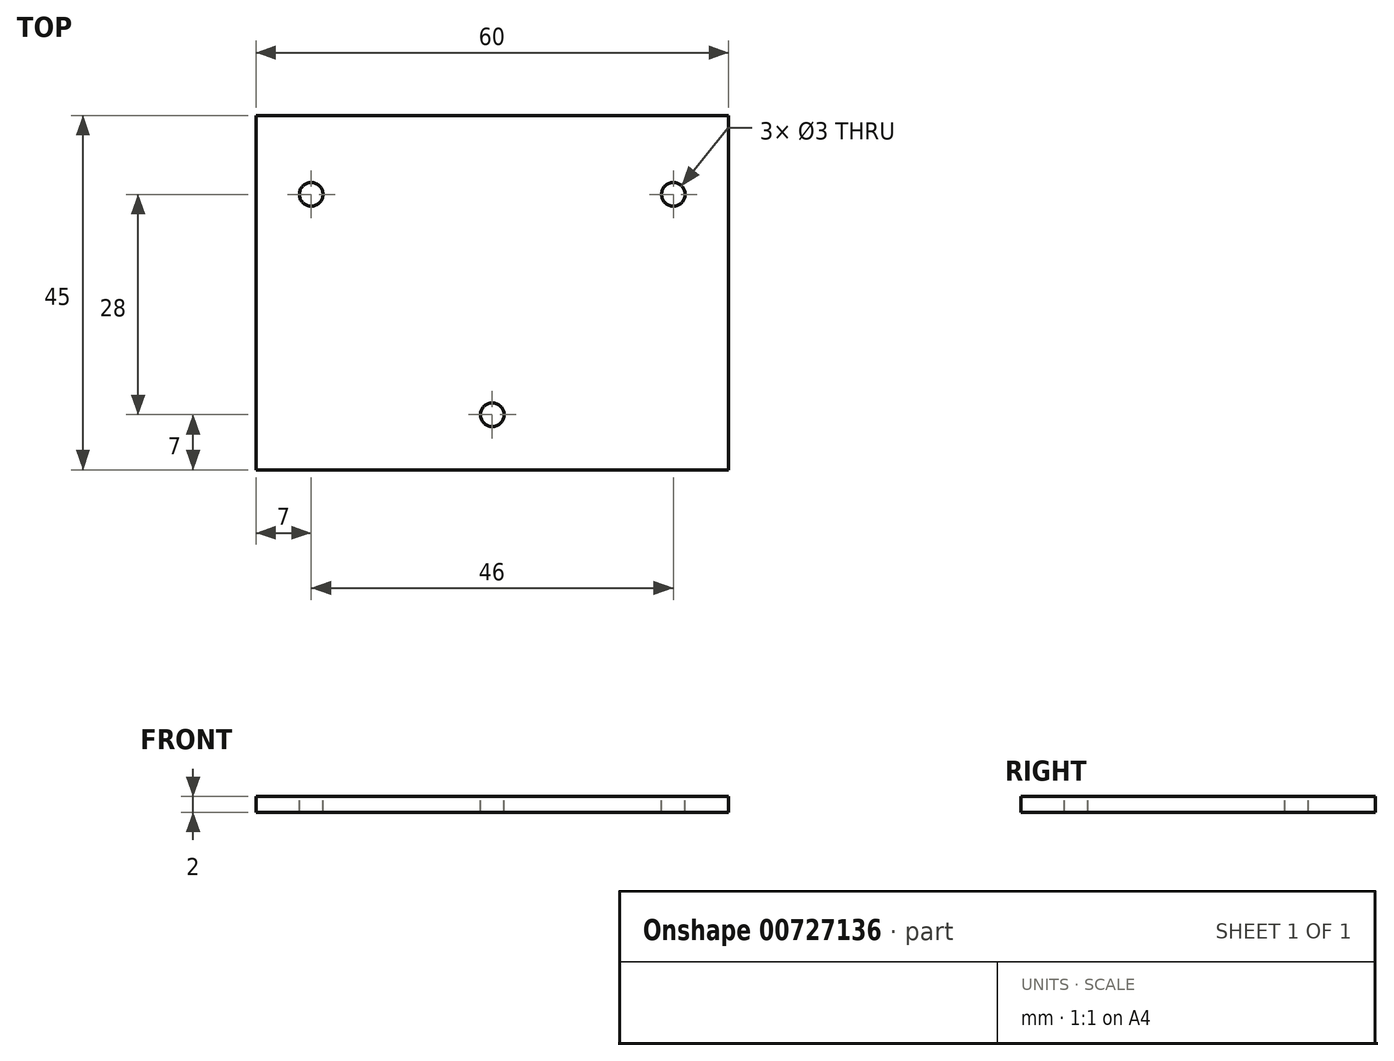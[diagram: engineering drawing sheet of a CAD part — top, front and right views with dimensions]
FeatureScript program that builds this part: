
annotation { "Feature Type Name" : "Feature", "Feature Type Description" : "" }
export const myFeature = defineFeature(function(context is Context, id is Id, definition is map)
    precondition{}
    {
        {
            var Q0;
            Q0=qCreatedBy(makeId("Top.planeOp"),FACE);
            var sketch = newSketch(context, id + "F0", { "sketchPlane" : qUnion([Q0])});
            skLineSegment(sketch, "E0.bottom", {"start": v(30, 22.5) * mm, "end": v(-30, 22.5) * mm});
            skLineSegment(sketch, "E0.top", {"start": v(30, -22.5) * mm, "end": v(-30, -22.5) * mm});
            skLineSegment(sketch, "E0.left", {"start": v(30, 22.5) * mm, "end": v(30, -22.5) * mm});
            skLineSegment(sketch, "E0.right", {"start": v(-30, 22.5) * mm, "end": v(-30, -22.5) * mm});
            skPoint(sketch, "E0.middle", {"position": v(0, 0) * mm});
            skSolve(sketch);
        }
        {
            var Q0;
            Q0 = qSketchRegion(id + "F0", true);
            extrude(context, id + "F1", {"entities" : qUnion([Q0]), "oppositeDirection" : true, "depth" : 2 * mm, "offsetDistance" : 25 * mm});
        }
        {
            var Q0;
            Q0=makeQuery(id+"F1.opExtrude","CAP_FACE",FACE,{"disambiguationData":[OSD([sQuery(id+"F0.wireOp",EDGE,"E0.bottom"),sQuery(id+"F0.wireOp",EDGE,"E0.top"),sQuery(id+"F0.wireOp",EDGE,"E0.left"),sQuery(id+"F0.wireOp",EDGE,"E0.right")])],"isStart":true});
            var sketch = newSketch(context, id + "F2", { "sketchPlane" : qUnion([Q0])});
            skLineSegment(sketch, "E1", {"start": v(0, -22.5) * mm, "end": v(0, 22.5) * mm});
            skLineSegment(sketch, "E2", {"start": v(-30, 22.5) * mm, "end": v(30, 22.5) * mm});
            skLineSegment(sketch, "E3.0", {"start": v(-30, 12.5) * mm, "end": v(30, 12.5) * mm});
            skLineSegment(sketch, "E4.0", {"start": v(-23, -22.5) * mm, "end": v(-23, 22.5) * mm});
            skCircle(sketch, "E5", {"center": v(-23, 12.5) * mm, "radius": 1.5 * mm});
            skLineSegment(sketch, "E6.0", {"start": v(-30, -15.5) * mm, "end": v(30, -15.5) * mm});
            skCircle(sketch, "E7", {"center": v(0, -15.5) * mm, "radius": 1.5 * mm});
            skCircle(sketch, "E8.MirrorC", {"center": v(23, 12.5) * mm, "radius": 1.5 * mm});
            skSolve(sketch);
        }
        {
            var Q0;
            Q0=sQuery(id+"F2.wireOp",VERTEX,"E5.center");
            var Q1;
            Q1=sQuery(id+"F2.wireOp",VERTEX,"E8.MirrorC.center");
            var Q2;
            Q2=sQuery(id+"F2.wireOp",VERTEX,"E7.center");
            var Q3;
            Q3=makeQuery(id+"F1.opExtrude","SWEPT_BODY",BODY,{"disambiguationData":[OSD([sQuery(id+"F0.wireOp",EDGE,"E0.bottom"),sQuery(id+"F0.wireOp",EDGE,"E0.top"),sQuery(id+"F0.wireOp",EDGE,"E0.left"),sQuery(id+"F0.wireOp",EDGE,"E0.right")])]});
            hole(context, id + "F3", {"style" : HoleStyle.SIMPLE, "endStyle" : HoleEndStyle.THROUGH, "standardTappedOrClearance" : lookupTablePath({ "standard" : "ISO", "size" : "3", "type" : "Drilled" }), "standardBlindInLast" : lookupTablePath({ "standard" : "ISO", "size" : "3", "type" : "Drilled" }), "holeDiameter" : 3 * mm, "majorDiameter" : 3 * mm, "isTappedThrough" : true, "tappedDepth" : 12 * mm, "tapClearance" : 3, "locations" : qUnion([Q0, Q1, Q2]), "scope" : qUnion([Q3])});
        }
    });
